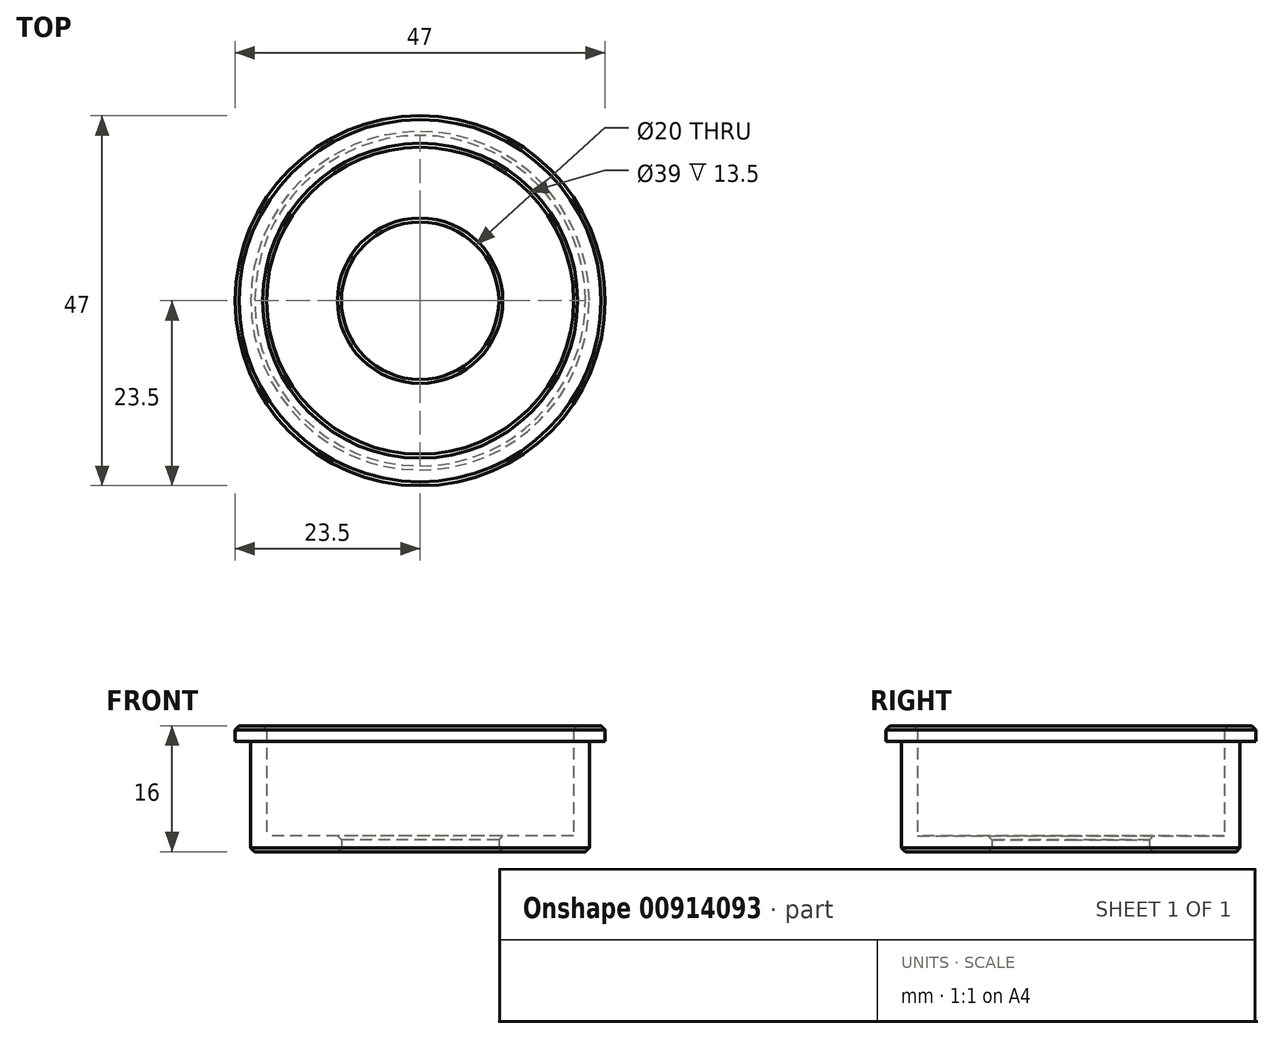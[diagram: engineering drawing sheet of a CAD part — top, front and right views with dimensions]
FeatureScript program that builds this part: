
annotation { "Feature Type Name" : "Feature", "Feature Type Description" : "" }
export const myFeature = defineFeature(function(context is Context, id is Id, definition is map)
    precondition{}
    {
        {
            var Q0;
            Q0=qCreatedBy(makeId("Top.planeOp"),FACE);
            var sketch = newSketch(context, id + "F0", { "sketchPlane" : qUnion([Q0])});
            skCircle(sketch, "E0", {"center": v(0, 0) * mm, "radius": 21.5 * mm});
            skCircle(sketch, "E1", {"center": v(0, 0) * mm, "radius": 10 * mm});
            skSolve(sketch);
        }
        {
            var Q0;
            Q0=makeQuery(id+"F0.imprint","IMPRINT",FACE,{"disambiguationData":[TD([[makeQuery(id+"F0.imprint","IMPRINT",EDGE,{"derivedFrom":sQuery(id+"F0.wireOp",EDGE,"E0")}),1.0]])]});
            extrude(context, id + "F1", {"entities" : qUnion([Q0]), "depth" : 2 * mm, "offsetDistance" : 25.4 * mm});
        }
        {
            var Q0;
            Q0=makeQuery(id+"F1.opExtrude","CAP_FACE",FACE,{"disambiguationData":[OSD([sQuery(id+"F0.wireOp",EDGE,"E0"),sQuery(id+"F0.wireOp",EDGE,"E1")])],"isStart":false});
            var sketch = newSketch(context, id + "F2", { "sketchPlane" : qUnion([Q0])});
            skCircle(sketch, "E2", {"center": v(0, 0) * mm, "radius": 21.5 * mm});
            skCircle(sketch, "E3", {"center": v(0, 0) * mm, "radius": 19.5 * mm});
            skSolve(sketch);
        }
        {
            var Q0;
            Q0=makeQuery(id+"F2.imprint","IMPRINT",FACE,{"disambiguationData":[TD([[makeQuery(id+"F2.imprint","IMPRINT",EDGE,{"derivedFrom":sQuery(id+"F2.wireOp",EDGE,"E2")}),1.0]])]});
            extrude(context, id + "F3", {"entities" : qUnion([Q0]), "operationType" : NewBodyOperationType.ADD, "depth" : 12 * mm, "offsetDistance" : 25.4 * mm});
        }
        {
            var Q0;
            Q0=makeQuery(id+"F3.opExtrude","CAP_FACE",FACE,{"disambiguationData":[OSD([sQuery(id+"F2.wireOp",EDGE,"E2"),sQuery(id+"F2.wireOp",EDGE,"E3")])],"isStart":false});
            var sketch = newSketch(context, id + "F4", { "sketchPlane" : qUnion([Q0])});
            skCircle(sketch, "E4", {"center": v(0, 0) * mm, "radius": 19.5 * mm});
            skCircle(sketch, "E5", {"center": v(0, 0) * mm, "radius": 23.5 * mm});
            skSolve(sketch);
        }
        {
            var Q0;
            Q0=makeQuery(id+"F4.imprint","IMPRINT",FACE,{"disambiguationData":[TD([[makeQuery(id+"F4.imprint","IMPRINT",EDGE,{"derivedFrom":sQuery(id+"F4.wireOp",EDGE,"E5")}),1.0]])]});
            var Q1;
            Q1=makeQuery(id+"F4.imprint","IMPRINT",FACE,{"disambiguationData":[TD([[makeQuery(id+"F4.imprint","IMPRINT",EDGE,{"derivedFrom":sQuery(id+"F4.wireOp",EDGE,"E4")}),-1.0]])]});
            extrude(context, id + "F5", {"entities" : qUnion([Q0, Q1]), "operationType" : NewBodyOperationType.ADD, "depth" : 2 * mm, "offsetDistance" : 25.4 * mm});
        }
        {
            var Q0;
            Q0=makeQuery(id+"F1.opExtrude","CAP_EDGE",EDGE,{"disambiguationData":[OSD([sQuery(id+"F0.wireOp",EDGE,"E0")])],"isStart":true});
            chamfer(context, id + "F6", {"entities" : qUnion([Q0]), "width" : 0.5 * mm, "tangentPropagation" : true});
        }
        {
            var Q0;
            Q0=makeQuery(id+"F1.opExtrude","CAP_EDGE",EDGE,{"disambiguationData":[OSD([sQuery(id+"F0.wireOp",EDGE,"E1")])],"isStart":false});
            var Q1;
            Q1=makeQuery(id+"F1.opExtrude","CAP_EDGE",EDGE,{"disambiguationData":[OSD([sQuery(id+"F0.wireOp",EDGE,"E1")])],"isStart":true});
            chamfer(context, id + "F7", {"entities" : qUnion([Q0, Q1]), "width" : 0.5 * mm, "tangentPropagation" : true});
        }
        {
            var Q0;
            Q0=makeQuery(id+"F5.opExtrude","CAP_EDGE",EDGE,{"disambiguationData":[OSD([sQuery(id+"F4.wireOp",EDGE,"E5")])],"isStart":false});
            var Q1;
            Q1=makeQuery(id+"F5.opExtrude","CAP_EDGE",EDGE,{"disambiguationData":[OSD([sQuery(id+"F4.wireOp",EDGE,"E4")])],"isStart":false});
            chamfer(context, id + "F8", {"entities" : qUnion([Q0, Q1]), "width" : 0.5 * mm, "tangentPropagation" : true});
        }
    });
